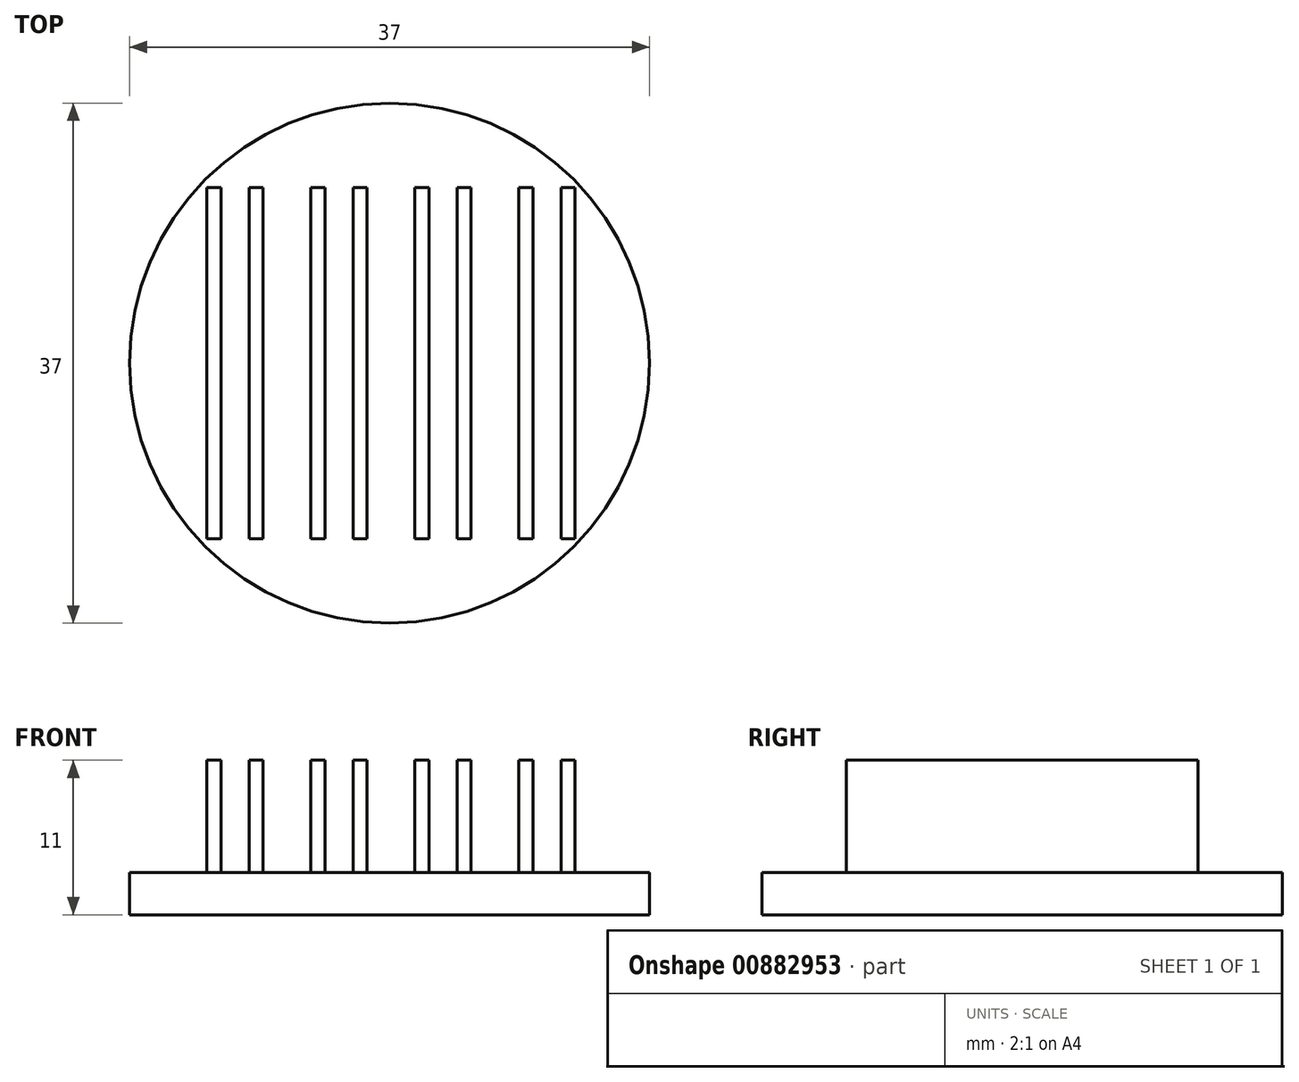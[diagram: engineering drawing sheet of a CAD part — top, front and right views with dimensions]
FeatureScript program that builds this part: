
annotation { "Feature Type Name" : "Feature", "Feature Type Description" : "" }
export const myFeature = defineFeature(function(context is Context, id is Id, definition is map)
    precondition{}
    {
        {
            var Q0;
            Q0=qCreatedBy(makeId("Top.planeOp"),FACE);
            var sketch = newSketch(context, id + "F0", { "sketchPlane" : qUnion([Q0])});
            skCircle(sketch, "E0", {"center": v(0, 0) * mm, "radius": 18.5 * mm});
            skSolve(sketch);
        }
        {
            var Q0;
            Q0 = qSketchRegion(id + "F0", true);
            extrude(context, id + "F1", {"entities" : qUnion([Q0]), "depth" : 3 * mm, "offsetDistance" : 25 * mm});
        }
        {
            var Q0;
            Q0=makeQuery(id+"F1.opExtrude","CAP_FACE",FACE,{"disambiguationData":[OSD([sQuery(id+"F0.wireOp",EDGE,"E0")])],"isStart":false});
            var sketch = newSketch(context, id + "F2", { "sketchPlane" : qUnion([Q0])});
            skLineSegment(sketch, "E1.bottom", {"start": v(-13, 12.5) * mm, "end": v(-12, 12.5) * mm});
            skLineSegment(sketch, "E1.top", {"start": v(-13, -12.5) * mm, "end": v(-12, -12.5) * mm});
            skLineSegment(sketch, "E1.left", {"start": v(-13, 12.5) * mm, "end": v(-13, -12.5) * mm});
            skLineSegment(sketch, "E1.right", {"start": v(-12, 12.5) * mm, "end": v(-12, -12.5) * mm});
            skPoint(sketch, "E2", {"position": v(-12, 0) * mm});
            skLineSegment(sketch, "E3.bottom", {"start": v(-10, 12.5) * mm, "end": v(-9, 12.5) * mm});
            skLineSegment(sketch, "E3.top", {"start": v(-10, -12.5) * mm, "end": v(-9, -12.5) * mm});
            skLineSegment(sketch, "E3.left", {"start": v(-10, 12.5) * mm, "end": v(-10, -12.5) * mm});
            skLineSegment(sketch, "E3.right", {"start": v(-9, 12.5) * mm, "end": v(-9, -12.5) * mm});
            skPoint(sketch, "E4", {"position": v(-10, 0) * mm});
            skLineSegment(sketch, "E5.1.0.0", {"start": v(-5.6, 12.5) * mm, "end": v(-4.6, 12.5) * mm});
            skLineSegment(sketch, "E5.1.0.1", {"start": v(-2.6, 12.5) * mm, "end": v(-1.6, 12.5) * mm});
            skLineSegment(sketch, "E5.1.0.2", {"start": v(-1.6, 12.5) * mm, "end": v(-1.6, -12.5) * mm});
            skLineSegment(sketch, "E5.1.0.3", {"start": v(-2.6, 12.5) * mm, "end": v(-2.6, -12.5) * mm});
            skLineSegment(sketch, "E5.1.0.4", {"start": v(-4.6, 12.5) * mm, "end": v(-4.6, -12.5) * mm});
            skLineSegment(sketch, "E5.1.0.5", {"start": v(-5.6, 12.5) * mm, "end": v(-5.6, -12.5) * mm});
            skLineSegment(sketch, "E5.1.0.6", {"start": v(-5.6, -12.5) * mm, "end": v(-4.6, -12.5) * mm});
            skLineSegment(sketch, "E5.1.0.7", {"start": v(-2.6, -12.5) * mm, "end": v(-1.6, -12.5) * mm});
            skLineSegment(sketch, "E5.2.0.0", {"start": v(1.8, 12.5) * mm, "end": v(2.8, 12.5) * mm});
            skLineSegment(sketch, "E5.2.0.1", {"start": v(4.8, 12.5) * mm, "end": v(5.8, 12.5) * mm});
            skLineSegment(sketch, "E5.2.0.2", {"start": v(5.8, 12.5) * mm, "end": v(5.8, -12.5) * mm});
            skLineSegment(sketch, "E5.2.0.3", {"start": v(4.8, 12.5) * mm, "end": v(4.8, -12.5) * mm});
            skLineSegment(sketch, "E5.2.0.4", {"start": v(2.8, 12.5) * mm, "end": v(2.8, -12.5) * mm});
            skLineSegment(sketch, "E5.2.0.5", {"start": v(1.8, 12.5) * mm, "end": v(1.8, -12.5) * mm});
            skLineSegment(sketch, "E5.2.0.6", {"start": v(1.8, -12.5) * mm, "end": v(2.8, -12.5) * mm});
            skLineSegment(sketch, "E5.2.0.7", {"start": v(4.8, -12.5) * mm, "end": v(5.8, -12.5) * mm});
            skLineSegment(sketch, "E5.3.0.0", {"start": v(9.2, 12.5) * mm, "end": v(10.2, 12.5) * mm});
            skLineSegment(sketch, "E5.3.0.1", {"start": v(12.2, 12.5) * mm, "end": v(13.2, 12.5) * mm});
            skLineSegment(sketch, "E5.3.0.2", {"start": v(13.2, 12.5) * mm, "end": v(13.2, -12.5) * mm});
            skLineSegment(sketch, "E5.3.0.3", {"start": v(12.2, 12.5) * mm, "end": v(12.2, -12.5) * mm});
            skLineSegment(sketch, "E5.3.0.4", {"start": v(10.2, 12.5) * mm, "end": v(10.2, -12.5) * mm});
            skLineSegment(sketch, "E5.3.0.5", {"start": v(9.2, 12.5) * mm, "end": v(9.2, -12.5) * mm});
            skLineSegment(sketch, "E5.3.0.6", {"start": v(9.2, -12.5) * mm, "end": v(10.2, -12.5) * mm});
            skLineSegment(sketch, "E5.3.0.7", {"start": v(12.2, -12.5) * mm, "end": v(13.2, -12.5) * mm});
            skLineSegment(sketch, "E5.direction1", {"start": v(-13, 12.5) * mm, "end": v(-5.6, 12.5) * mm, "construction": true});
            skSolve(sketch);
        }
        {
            var Q0;
            Q0 = qSketchRegion(id + "F2", true);
            extrude(context, id + "F3", {"entities" : qUnion([Q0]), "operationType" : NewBodyOperationType.ADD, "depth" : 8 * mm, "offsetDistance" : 25 * mm});
        }
    });
